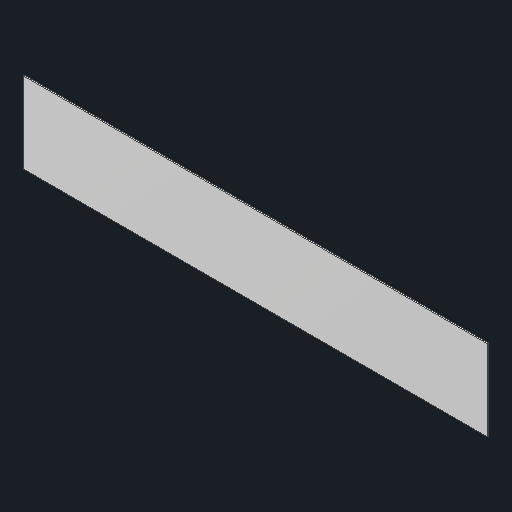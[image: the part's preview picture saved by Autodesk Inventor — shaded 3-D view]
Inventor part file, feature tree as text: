
AUTODESK INVENTOR PART (.ipt)
format: ipt  version: 2024 (Build 280153000, 153)  size: 82,432 bytes
history: native  units: in
note: dims shown in document units (in); Inventor stores cm internally (conversion verified against a paired STEP export)
features: extrude x1
ambient origin geometry x8: Origin, YZ Plane, XZ Plane, XY Plane, X Axis, Y Axis, Z Axis, Center Point
bodies: Solid1 (feature_tree)
feature tree (1):
  extrude  "Extrude1"  [1 undecoded]
note: 1 required parameter value undecoded (feature->parameter linkage not recoverable at this tier; creation-order binding heuristic only, values carry confidence <= 0.55)
